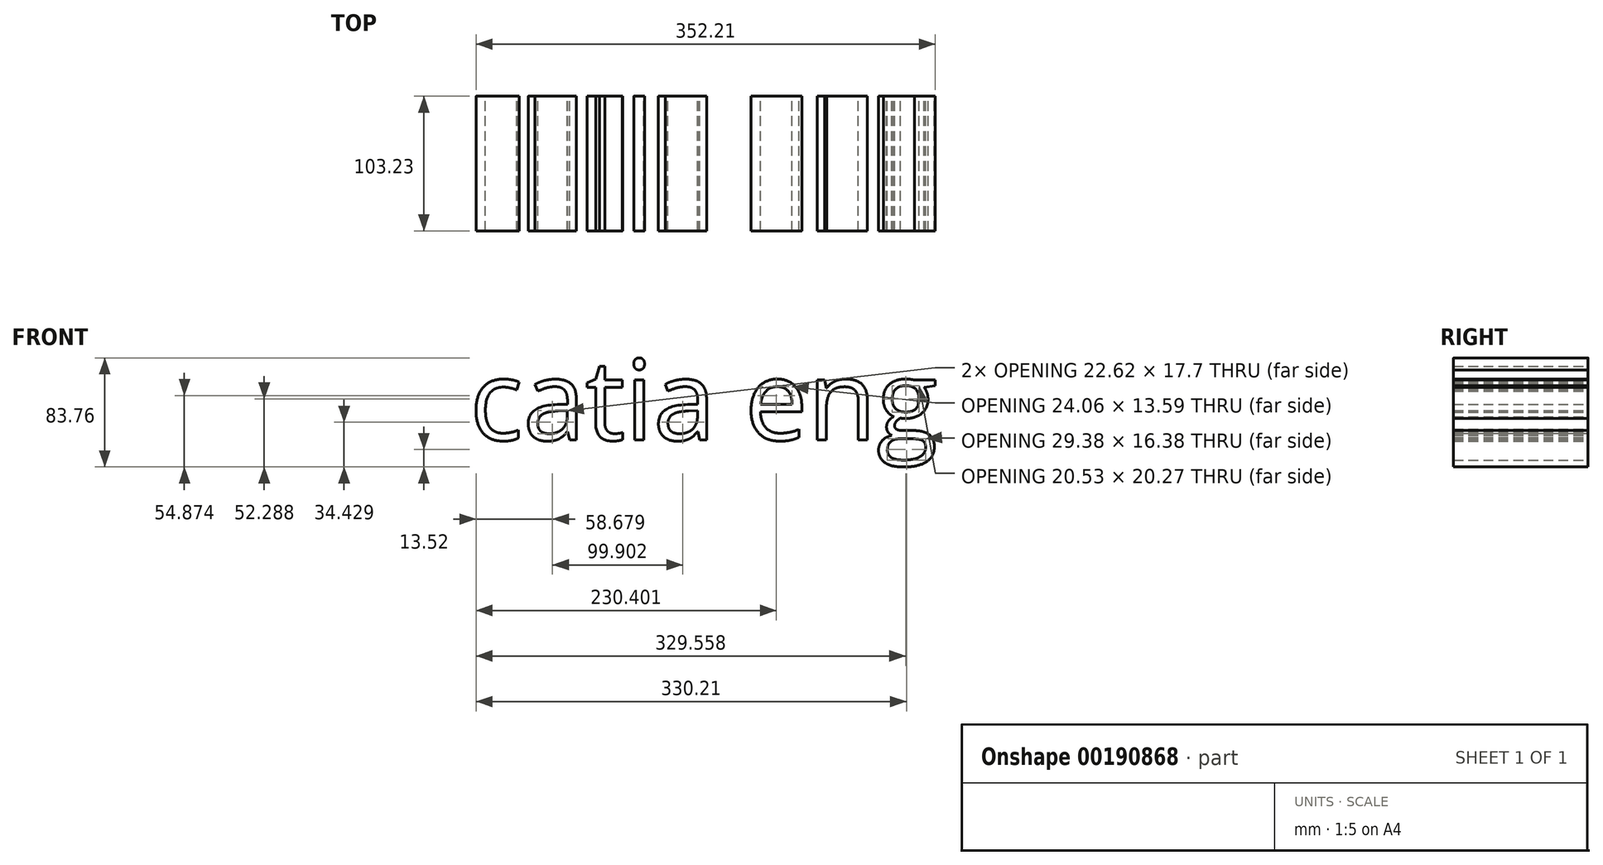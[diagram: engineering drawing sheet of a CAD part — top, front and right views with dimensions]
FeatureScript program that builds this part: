
annotation { "Feature Type Name" : "Feature", "Feature Type Description" : "" }
export const myFeature = defineFeature(function(context is Context, id is Id, definition is map)
    precondition{}
    {
        {
            var Q0;
            Q0=qCreatedBy(makeId("Front.planeOp"),FACE);
            var sketch = newSketch(context, id + "F2", { "sketchPlane" : qUnion([Q0])});
            skText(sketch, "E0", { "text": "catia eng", "fontName": "OpenSans-Regular.ttf"});
            const initialGuessFRF5MYYFEUTh7rIvF_0  = {"E0": [0.06689, 0.0265, 1, 0, 0.0619]};
            skSetInitialGuess(sketch, initialGuessFRF5MYYFEUTh7rIvF_0);
            skSolve(sketch);
        }
        {
            var Q0;
            Q0 = qSketchRegion(id + "F2", true);
            extrude(context, id + "F0", {"entities" : qUnion([Q0]), "depth" : 103.23 * mm});
        }
        {
            var Q0;
            Q0=qCreatedBy(makeId("Top.planeOp"),FACE);
            var sketch = newSketch(context, id + "F1", { "sketchPlane" : qUnion([Q0])});
            skFitSpline(sketch, "E1", {"points": [v(440.35, 0) * mm, v(325.82, -52.4) * mm, v(230.62, -26.2) * mm, v(134.74, -62.58) * mm, v(44.53, -32.3) * mm], "startDerivative": vector(-425.92, -300.78) * mm, "endDerivative": vector(-377.07, 222.76) * mm});
            skSolve(sketch);
        }
        {
            var Q0;
            Q0=sQuery(id+"F1.wireOp",EDGE,"E1");
            extrude(context, id + "F3", {"bodyType" : ToolBodyType.SURFACE, "surfaceEntities" : qUnion([Q0]), "depth" : 342.28 * mm});
        }
    });
